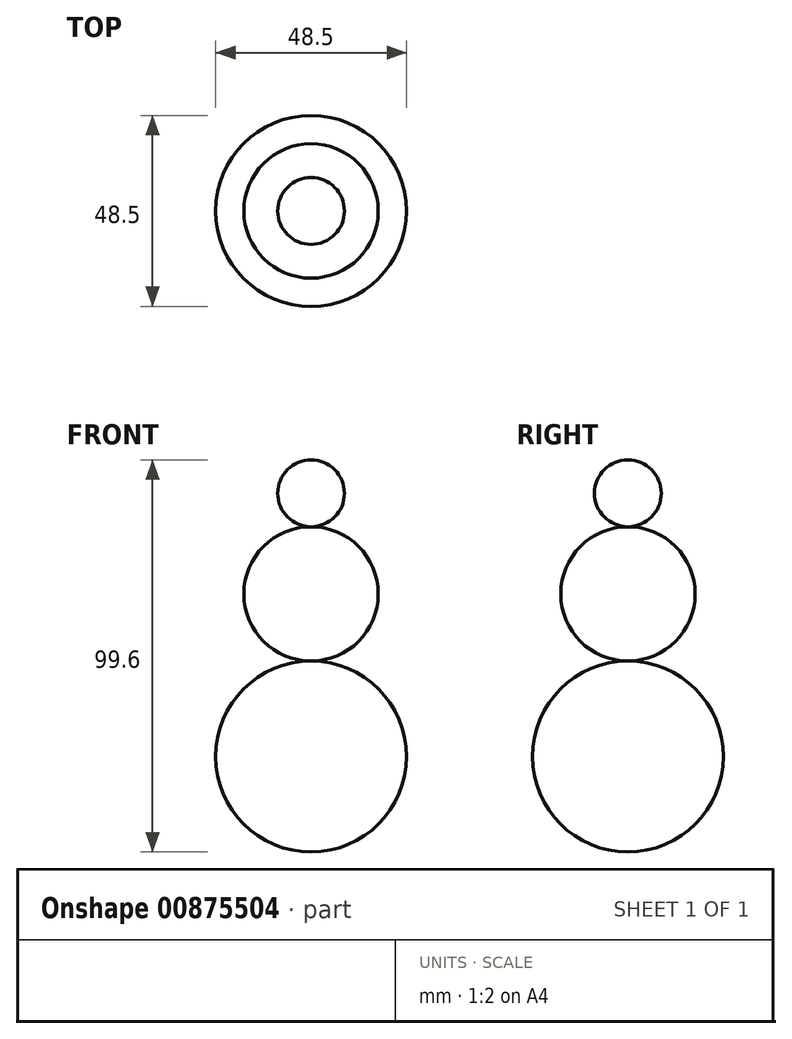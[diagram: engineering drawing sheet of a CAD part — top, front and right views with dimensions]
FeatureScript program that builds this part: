
annotation { "Feature Type Name" : "Feature", "Feature Type Description" : "" }
export const myFeature = defineFeature(function(context is Context, id is Id, definition is map)
    precondition{}
    {
        {
            var Q0;
            Q0=qCreatedBy(makeId("Front.planeOp"),FACE);
            var sketch = newSketch(context, id + "F0", { "sketchPlane" : qUnion([Q0])});
            skCircle(sketch, "E0", {"center": v(0, 0) * mm, "radius": 24.25 * mm});
            skCircle(sketch, "E1", {"center": v(0, 41.32) * mm, "radius": 17.07 * mm});
            skPoint(sketch, "E1.first.point", {"position": v(0, 24.25) * mm});
            skPoint(sketch, "E1.second.point", {"position": v(-15.69, 48.03) * mm});
            skPoint(sketch, "E1.third.point", {"position": v(15.92, 47.47) * mm});
            skCircle(sketch, "E2", {"center": v(0, 66.86) * mm, "radius": 8.48 * mm});
            skPoint(sketch, "E2.first.point", {"position": v(0, 58.38) * mm});
            skPoint(sketch, "E2.second.point", {"position": v(-6.47, 72.34) * mm});
            skPoint(sketch, "E2.third.point", {"position": v(5.34, 73.45) * mm});
            skLineSegment(sketch, "E3", {"start": v(0, 75.35) * mm, "end": v(0, -24.25) * mm});
            skSolve(sketch);
        }
        {
            var Q0;
            Q0=qCreatedBy(makeId("Front.planeOp"),FACE);
            var sketch = newSketch(context, id + "F1", { "sketchPlane" : qUnion([Q0])});
            skLineSegment(sketch, "E4", {"start": v(0, 67.35) * mm, "end": v(0, 0) * mm});
            skSolve(sketch);
        }
        {
            var Q0;
            {var subQ0=sQuery(id+"F0.wireOp",EDGE,"E3");var subQ1=sQuery(id+"F0.wireOp",EDGE,"E2");var subQ2=makeQuery(id+"F0.imprint","INTERSECT",VERTEX,{"derivedFrom":[subQ1,subQ0]});Q0=makeQuery(id+"F0.imprint","IMPRINT",FACE,{"disambiguationData":[TD([[makeQuery(id+"F0.imprint","IMPRINT",EDGE,{"disambiguationData":[TD([[subQ2,1.0]])],"derivedFrom":subQ1}),1.0]])]});}
            var Q1;
            {var subQ0=sQuery(id+"F0.wireOp",EDGE,"E3");var subQ1=sQuery(id+"F0.wireOp",EDGE,"E1");var subQ2=makeQuery(id+"F0.imprint","INTERSECT",VERTEX,{"derivedFrom":[sQuery(id+"F0.wireOp",EDGE,"E0"),subQ1,subQ0]});Q1=makeQuery(id+"F0.imprint","IMPRINT",FACE,{"disambiguationData":[TD([[makeQuery(id+"F0.imprint","IMPRINT",EDGE,{"disambiguationData":[TD([[subQ2,-1.0]])],"derivedFrom":subQ1}),1.0]])]});}
            var Q2;
            {var subQ0=sQuery(id+"F0.wireOp",EDGE,"E3");var subQ1=sQuery(id+"F0.wireOp",EDGE,"E0");var subQ2=makeQuery(id+"F0.imprint","INTERSECT",VERTEX,{"derivedFrom":[subQ1,subQ0]});Q2=makeQuery(id+"F0.imprint","IMPRINT",FACE,{"disambiguationData":[TD([[makeQuery(id+"F0.imprint","IMPRINT",EDGE,{"disambiguationData":[TD([[subQ2,-1.0]])],"derivedFrom":subQ1}),1.0]])]});}
            var Q3;
            Q3=sQuery(id+"F1.wireOp",EDGE,"E4");
            revolve(context, id + "F2", {"surfaceOperationType" : NewSurfaceOperationType.NEW, "entities" : qUnion([Q0, Q1, Q2]), "axis" : qUnion([Q3]), "revolveType" : RevolveType.FULL});
        }
    });
